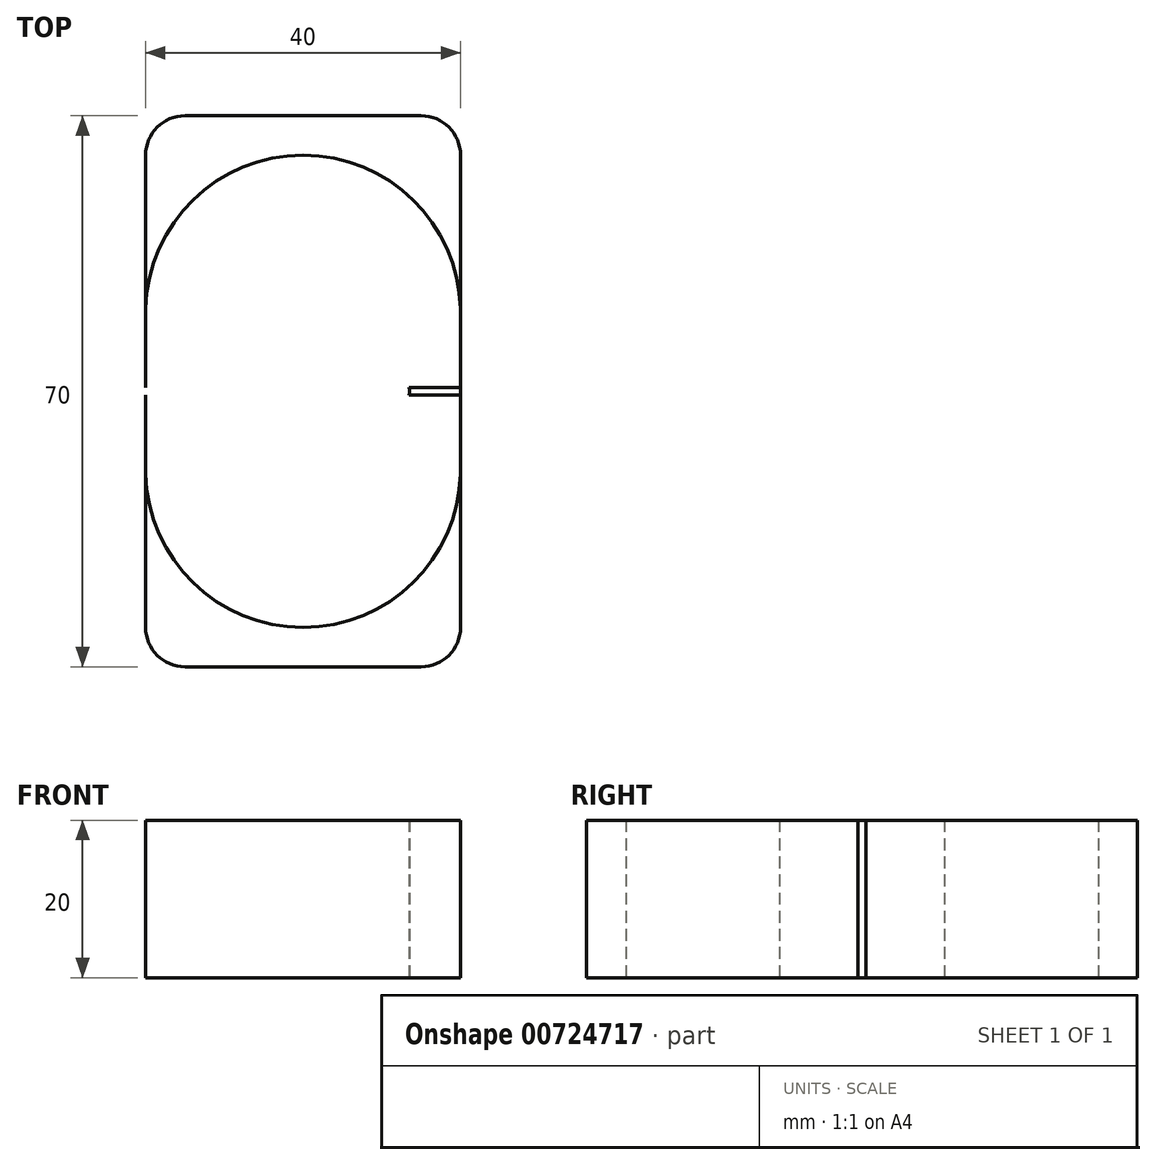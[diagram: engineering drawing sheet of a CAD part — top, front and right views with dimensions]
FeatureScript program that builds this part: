
annotation { "Feature Type Name" : "Feature", "Feature Type Description" : "" }
export const myFeature = defineFeature(function(context is Context, id is Id, definition is map)
    precondition{}
    {
        {
            var Q0;
            Q0=qCreatedBy(makeId("Top.planeOp"),FACE);
            var sketch = newSketch(context, id + "F0", { "sketchPlane" : qUnion([Q0])});
            skCircle(sketch, "E0", {"center": v(0, 0) * mm, "radius": 13.5 * mm});
            skCircle(sketch, "E1", {"center": v(0, 0) * mm, "radius": 20 * mm});
            skLineSegment(sketch, "E2.bottom", {"start": v(21.11, -0.5) * mm, "end": v(-21.11, -0.5) * mm});
            skLineSegment(sketch, "E2.top", {"start": v(21.11, 0.5) * mm, "end": v(-21.11, 0.5) * mm});
            skLineSegment(sketch, "E2.left", {"start": v(21.11, -0.5) * mm, "end": v(21.11, 0.5) * mm});
            skLineSegment(sketch, "E2.right", {"start": v(-21.11, -0.5) * mm, "end": v(-21.11, 0.5) * mm});
            skLineSegment(sketch, "E3.bottom", {"start": v(20, -25) * mm, "end": v(-20, -25) * mm});
            skLineSegment(sketch, "E3.top", {"start": v(20, 25) * mm, "end": v(-20, 25) * mm});
            skLineSegment(sketch, "E3.left", {"start": v(20, -25) * mm, "end": v(20, 25) * mm});
            skLineSegment(sketch, "E3.right", {"start": v(-20, -25) * mm, "end": v(-20, 25) * mm});
            skSolve(sketch);
        }
        {
            var Q0;
            {var subQ0=sQuery(id+"F0.wireOp",EDGE,"E2.top");var subQ1=sQuery(id+"F0.wireOp",EDGE,"E0");var subQ2=makeQuery(id+"F0.imprint","INTERSECT",VERTEX,{"disambiguationData":[OD(0.0)],"derivedFrom":[subQ1,subQ0]});Q0=makeQuery(id+"F0.imprint","IMPRINT",FACE,{"disambiguationData":[TD([[makeQuery(id+"F0.imprint","IMPRINT",EDGE,{"disambiguationData":[TD([[subQ2,1.0]])],"derivedFrom":subQ1}),-1.0]])]});}
            var Q1;
            {var subQ0=sQuery(id+"F0.wireOp",EDGE,"E2.bottom");var subQ1=sQuery(id+"F0.wireOp",EDGE,"E0");var subQ2=makeQuery(id+"F0.imprint","INTERSECT",VERTEX,{"disambiguationData":[OD(0.0)],"derivedFrom":[subQ1,subQ0]});Q1=makeQuery(id+"F0.imprint","IMPRINT",FACE,{"disambiguationData":[TD([[makeQuery(id+"F0.imprint","IMPRINT",EDGE,{"disambiguationData":[TD([[subQ2,-1.0]])],"derivedFrom":subQ1}),-1.0]])]});}
            var Q2;
            {var subQ5=sQuery(id+"F0.wireOp",EDGE,"E3.bottom");Q2=makeQuery(id+"F0.imprint","IMPRINT",FACE,{"disambiguationData":[TD([[makeQuery(id+"F0.imprint","IMPRINT",EDGE,{"derivedFrom":subQ5}),-1.0]])]});}
            var Q3;
            {var subQ0=sQuery(id+"F0.wireOp",EDGE,"E3.top");Q3=makeQuery(id+"F0.imprint","IMPRINT",FACE,{"disambiguationData":[TD([[makeQuery(id+"F0.imprint","IMPRINT",EDGE,{"derivedFrom":subQ0}),1.0]])]});}
            extrude(context, id + "F1", {"entities" : qUnion([Q0, Q1, Q2, Q3]), "depth" : 20 * mm, "offsetDistance" : 25 * mm});
        }
        {
            var Q0;
            Q0=makeQuery(id+"F1.opExtrude","SWEPT_EDGE",EDGE,{"disambiguationData":[OSD([sQuery(id+"F0.wireOp",EDGE,"E3.bottom"),sQuery(id+"F0.wireOp",EDGE,"E3.left")])]});
            var Q1;
            Q1=makeQuery(id+"F1.opExtrude","SWEPT_EDGE",EDGE,{"disambiguationData":[OSD([sQuery(id+"F0.wireOp",EDGE,"E3.bottom"),sQuery(id+"F0.wireOp",EDGE,"E3.right")])]});
            var Q2;
            Q2=makeQuery(id+"F1.opExtrude","SWEPT_EDGE",EDGE,{"disambiguationData":[OSD([sQuery(id+"F0.wireOp",EDGE,"E3.top"),sQuery(id+"F0.wireOp",EDGE,"E3.left")])]});
            var Q3;
            Q3=makeQuery(id+"F1.opExtrude","SWEPT_EDGE",EDGE,{"disambiguationData":[OSD([sQuery(id+"F0.wireOp",EDGE,"E3.top"),sQuery(id+"F0.wireOp",EDGE,"E3.right")])]});
            fillet(context, id + "F2", {"entities" : qUnion([Q0, Q1, Q2, Q3]), "radius" : 5 * mm, "tangentPropagation" : true, "allowEdgeOverflow" : false});
        }
        {
            var Q0;
            Q0=makeQuery(id+"F1.opExtrude","SWEPT_BODY",BODY,{"disambiguationData":[OSD([sQuery(id+"F0.wireOp",EDGE,"E0"),sQuery(id+"F0.wireOp",EDGE,"E2.bottom"),sQuery(id+"F0.wireOp",EDGE,"E3.bottom"),sQuery(id+"F0.wireOp",EDGE,"E3.left"),sQuery(id+"F0.wireOp",EDGE,"E3.right")])]});
            transform(context, id + "F3", {"entities" : qUnion([Q0]), "transformType" : TransformType.TRANSLATION_3D, "dx" : 0 * mm, "dy" : -10 * mm, "dz" : 0 * mm, "makeCopy" : false});
        }
        {
            var Q0;
            Q0=makeQuery(id+"F1.opExtrude","SWEPT_BODY",BODY,{"disambiguationData":[OSD([sQuery(id+"F0.wireOp",EDGE,"E0"),sQuery(id+"F0.wireOp",EDGE,"E2.top"),sQuery(id+"F0.wireOp",EDGE,"E3.top"),sQuery(id+"F0.wireOp",EDGE,"E3.left"),sQuery(id+"F0.wireOp",EDGE,"E3.right")])]});
            transform(context, id + "F4", {"entities" : qUnion([Q0]), "transformType" : TransformType.TRANSLATION_3D, "dx" : 0 * mm, "dy" : 10 * mm, "dz" : 0 * mm, "makeCopy" : false});
        }
        {
            var Q0;
            {var subQ0=sQuery(id+"F0.wireOp",EDGE,"E2.bottom");Q0=makeQuery(id+"F1.opExtrude","SWEPT_FACE",FACE,{"disambiguationData":[OSD([subQ0]),TDD([makeQuery(id+"F0.imprint","IMPRINT",EDGE,{"disambiguationData":[TD([[makeQuery(id+"F0.imprint","INTERSECT",VERTEX,{"derivedFrom":[subQ0,sQuery(id+"F0.wireOp",EDGE,"E3.left")]}),-1.0]])],"derivedFrom":subQ0}),makeQuery(id+"F0.imprint","IMPRINT",EDGE,{"disambiguationData":[TD([[makeQuery(id+"F0.imprint","INTERSECT",VERTEX,{"disambiguationData":[OD(1.0)],"derivedFrom":[sQuery(id+"F0.wireOp",EDGE,"E0"),subQ0]}),1.0]])],"derivedFrom":subQ0})])]});}
            var Q1;
            {var subQ0=sQuery(id+"F0.wireOp",EDGE,"E2.bottom");Q1=makeQuery(id+"F1.opExtrude","SWEPT_FACE",FACE,{"disambiguationData":[OSD([subQ0]),TDD([makeQuery(id+"F0.imprint","IMPRINT",EDGE,{"disambiguationData":[TD([[makeQuery(id+"F0.imprint","INTERSECT",VERTEX,{"disambiguationData":[OD(0.0)],"derivedFrom":[sQuery(id+"F0.wireOp",EDGE,"E0"),subQ0]}),-1.0]])],"derivedFrom":subQ0}),makeQuery(id+"F0.imprint","IMPRINT",EDGE,{"disambiguationData":[TD([[makeQuery(id+"F0.imprint","INTERSECT",VERTEX,{"derivedFrom":[subQ0,sQuery(id+"F0.wireOp",EDGE,"E3.right")]}),1.0]])],"derivedFrom":subQ0})])]});}
            extrude(context, id + "F5", {"entities" : qUnion([Q0, Q1]), "operationType" : NewBodyOperationType.ADD, "depth" : 10 * mm, "offsetDistance" : 25 * mm});
        }
        {
            var Q0;
            {var subQ0=sQuery(id+"F0.wireOp",EDGE,"E2.top");Q0=makeQuery(id+"F1.opExtrude","SWEPT_FACE",FACE,{"disambiguationData":[OSD([subQ0]),TDD([makeQuery(id+"F0.imprint","IMPRINT",EDGE,{"disambiguationData":[TD([[makeQuery(id+"F0.imprint","INTERSECT",VERTEX,{"disambiguationData":[OD(0.0)],"derivedFrom":[sQuery(id+"F0.wireOp",EDGE,"E0"),subQ0]}),-1.0]])],"derivedFrom":subQ0}),makeQuery(id+"F0.imprint","IMPRINT",EDGE,{"disambiguationData":[TD([[makeQuery(id+"F0.imprint","INTERSECT",VERTEX,{"derivedFrom":[subQ0,sQuery(id+"F0.wireOp",EDGE,"E3.right")]}),1.0]])],"derivedFrom":subQ0})])]});}
            var Q1;
            {var subQ0=sQuery(id+"F0.wireOp",EDGE,"E2.top");Q1=makeQuery(id+"F1.opExtrude","SWEPT_FACE",FACE,{"disambiguationData":[OSD([subQ0]),TDD([makeQuery(id+"F0.imprint","IMPRINT",EDGE,{"disambiguationData":[TD([[makeQuery(id+"F0.imprint","INTERSECT",VERTEX,{"derivedFrom":[subQ0,sQuery(id+"F0.wireOp",EDGE,"E3.left")]}),-1.0]])],"derivedFrom":subQ0}),makeQuery(id+"F0.imprint","IMPRINT",EDGE,{"disambiguationData":[TD([[makeQuery(id+"F0.imprint","INTERSECT",VERTEX,{"disambiguationData":[OD(1.0)],"derivedFrom":[sQuery(id+"F0.wireOp",EDGE,"E0"),subQ0]}),1.0]])],"derivedFrom":subQ0})])]});}
            extrude(context, id + "F6", {"entities" : qUnion([Q0, Q1]), "operationType" : NewBodyOperationType.ADD, "depth" : 10 * mm, "offsetDistance" : 25 * mm});
        }
    });
